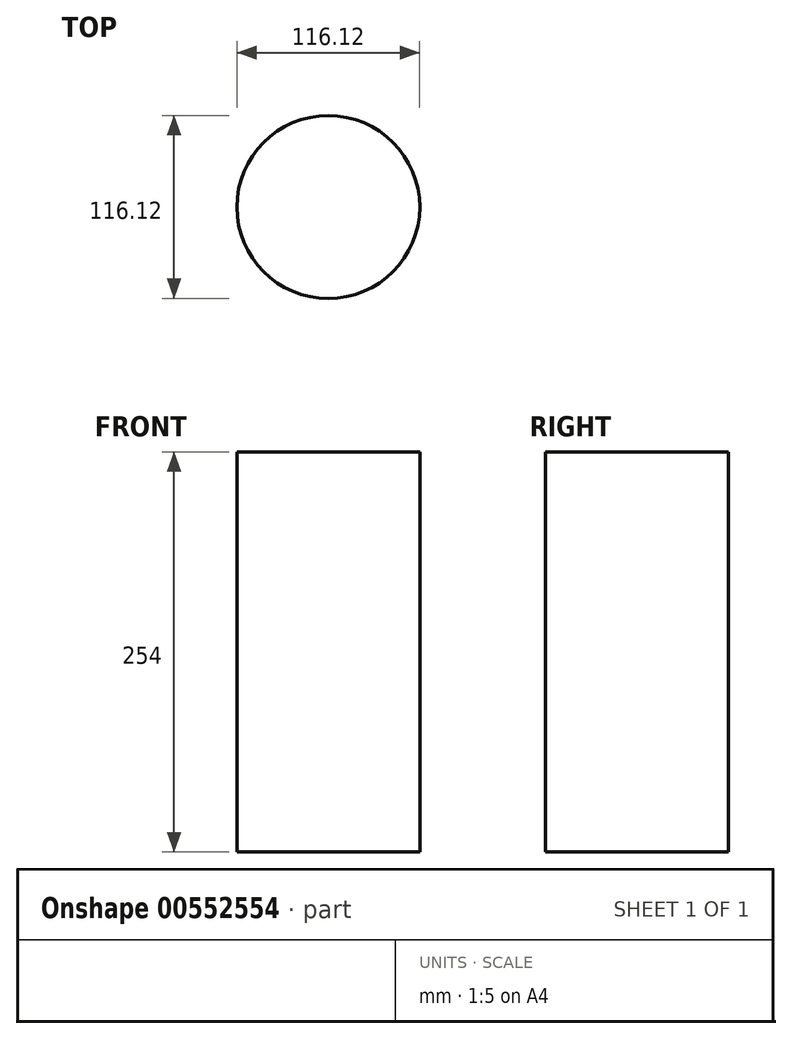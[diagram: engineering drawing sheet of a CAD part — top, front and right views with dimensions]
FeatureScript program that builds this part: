
annotation { "Feature Type Name" : "Feature", "Feature Type Description" : "" }
export const myFeature = defineFeature(function(context is Context, id is Id, definition is map)
    precondition{}
    {
        {
            var Q0;
            Q0=qCreatedBy(makeId("Top.planeOp"),FACE);
            var sketch = newSketch(context, id + "F0", { "sketchPlane" : qUnion([Q0])});
            skCircle(sketch, "E0", {"center": v(0, 0) * mm, "radius": 58.06 * mm});
            skSolve(sketch);
        }
        {
            var Q0;
            Q0 = qSketchRegion(id + "F0", true);
            extrude(context, id + "F1", {"entities" : qUnion([Q0]), "depth" : 254 * mm, "offsetDistance" : 25.4 * mm});
        }
    });
